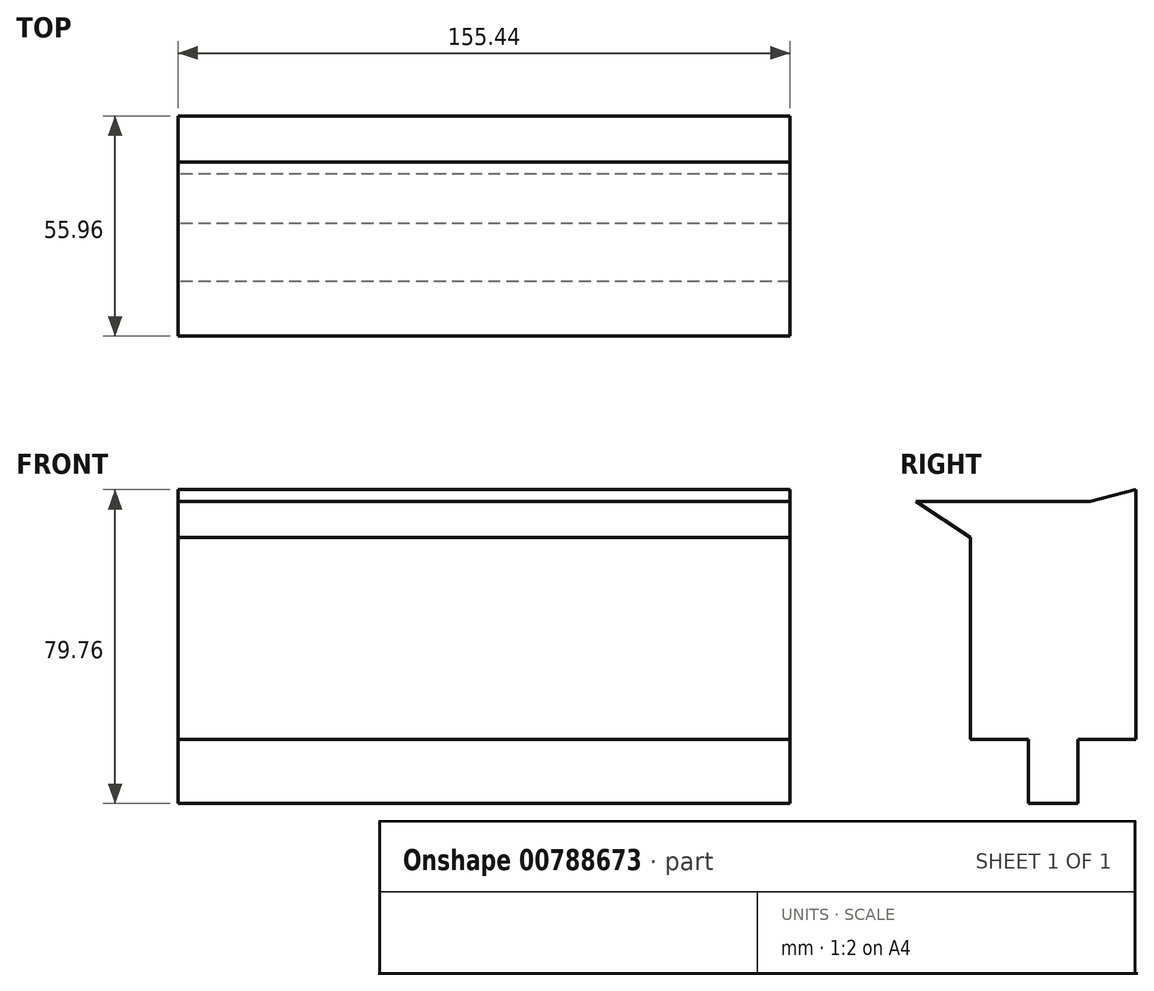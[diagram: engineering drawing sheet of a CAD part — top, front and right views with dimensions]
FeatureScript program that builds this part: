
annotation { "Feature Type Name" : "Feature", "Feature Type Description" : "" }
export const myFeature = defineFeature(function(context is Context, id is Id, definition is map)
    precondition{}
    {
        {
            var Q0;
            Q0=qCreatedBy(makeId("Right.planeOp"),FACE);
            var sketch = newSketch(context, id + "F0", { "sketchPlane" : qUnion([Q0])});
            skLineSegment(sketch, "E0.bottom", {"start": v(6.29, -39.88) * mm, "end": v(-6.29, -39.88) * mm});
            skLineSegment(sketch, "E0.left", {"start": v(21.06, -23.62) * mm, "end": v(21.06, 36.83) * mm});
            skPoint(sketch, "E0.middle", {"position": v(0, 0) * mm});
            skLineSegment(sketch, "E1.left", {"start": v(6.29, -23.62) * mm, "end": v(6.29, -39.88) * mm});
            skLineSegment(sketch, "E1.right", {"start": v(-6.29, -23.62) * mm, "end": v(-6.29, -39.88) * mm});
            skLineSegment(sketch, "E2", {"start": v(-6.29, -23.62) * mm, "end": v(-21.06, -23.62) * mm});
            skLineSegment(sketch, "E3", {"start": v(6.29, -23.62) * mm, "end": v(21.06, -23.62) * mm});
            skLineSegment(sketch, "E4.right", {"start": v(-21.06, -23.62) * mm, "end": v(-21.06, 27.69) * mm});
            skLineSegment(sketch, "E5", {"start": v(-21.06, 27.69) * mm, "end": v(-34.9, 36.83) * mm});
            skLineSegment(sketch, "E6", {"start": v(9.3, 36.83) * mm, "end": v(-34.9, 36.83) * mm});
            skLineSegment(sketch, "E7", {"start": v(21.06, 36.83) * mm, "end": v(21.06, 39.88) * mm});
            skLineSegment(sketch, "E8", {"start": v(21.06, 39.88) * mm, "end": v(9.3, 36.83) * mm});
            skSolve(sketch);
        }
        {
            var Q0;
            Q0=qSketchRegion(id+"F0",true);
            extrude(context, id + "F1", {"entities" : qUnion([Q0]), "endBound" : BoundingType.SYMMETRIC, "depth" : 155.45 * mm, "offsetDistance" : 25.4 * mm});
        }
    });
